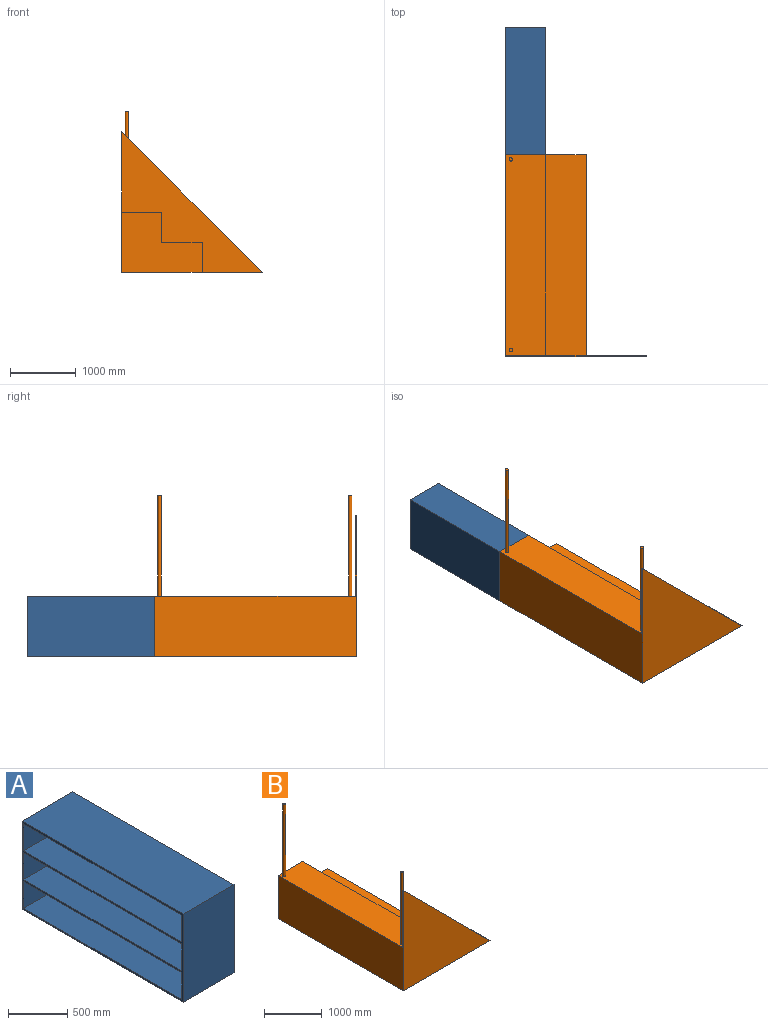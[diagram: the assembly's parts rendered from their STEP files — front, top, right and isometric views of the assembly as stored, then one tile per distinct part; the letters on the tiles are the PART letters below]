
ASSEMBLY  parts=2 mates=1
PART A: 21 faces, bbox 609.6x1930.4x914.4 mm
  f0: plane 1930.4x914.4mm, normal (-1,0,0), area 179031.9mm2, adj f1,f3,f4,f5,f6,f7,f8,f9
  f1: plane 1930.4x609.6mm, normal (0,0,-1), area 1176771.8mm2, adj f0,f2,f4,f5
  f2: plane 1930.4x914.4mm, normal (1,0,0), area 1765157.8mm2, adj f1,f3,f4,f5
  f3: plane 1930.4x609.6mm, normal (0,0,1), area 1176771.8mm2, adj f0,f2,f4,f5
  f4: plane 914.4x609.6mm, normal (0,-1,0), area 557418.2mm2, adj f0,f1,f2,f3
  f5: plane 914.4x609.6mm, normal (0,1,0), area 557418.2mm2, adj f0,f1,f2,f3
  f6: plane 1892.3x590.55mm, normal (0,0,-1), area 1117497.8mm2, adj f0,f7,f9,f10
  f7: plane 590.55x279.4mm, normal (0,-1,0), area 164999.7mm2, adj f0,f6,f8,f10
  f8: plane 1892.3x590.55mm, normal (0,0,1), area 1117497.8mm2, adj f0,f7,f9,f10
  f9: plane 590.55x279.4mm, normal (0,1,0), area 164999.7mm2, adj f0,f6,f8,f10
  f10: plane 1892.3x279.4mm, normal (-1,0,0), area 528708.6mm2, adj f6,f7,f8,f9
  f11: plane 1892.3x590.55mm, normal (0,0,-1), area 1117497.8mm2, adj f0,f12,f14,f15
  f12: plane 590.55x279.4mm, normal (0,-1,0), area 164999.7mm2, adj f0,f11,f13,f15
  f13: plane 1892.3x590.55mm, normal (0,0,1), area 1117497.8mm2, adj f0,f12,f14,f15
  f14: plane 590.55x279.4mm, normal (0,1,0), area 164999.7mm2, adj f0,f11,f13,f15
  f15: plane 1892.3x279.4mm, normal (-1,0,0), area 528708.6mm2, adj f11,f12,f13,f14
  f16: plane 1892.3x590.55mm, normal (0,0,-1), area 1117497.8mm2, adj f0,f17,f19,f20
  f17: plane 590.55x279.4mm, normal (0,-1,0), area 164999.7mm2, adj f0,f16,f18,f20
  f18: plane 1892.3x590.55mm, normal (0,0,1), area 1117497.8mm2, adj f0,f17,f19,f20
  f19: plane 590.55x279.4mm, normal (0,1,0), area 164999.7mm2, adj f0,f16,f18,f20
  f20: plane 1892.3x279.4mm, normal (-1,0,0), area 528708.6mm2, adj f16,f17,f18,f19
PART B: 14 faces, bbox 2133.6x3067.1x2438.4 mm
  f0: plane 3067.05x2133.6mm, normal (-1,0,0), area 2827736.3mm2, adj f1,f5,f6,f11,f12,f13
  f1: plane 3067.05x2133.6mm, normal (0,0,-1), area 3756766.7mm2, adj f0,f2,f6,f11,f12,f13
  f2: plane 3048x457.2mm, normal (1,0,0), area 1393545.6mm2, adj f1,f3,f6,f13
  f3: plane 3048x609.6mm, normal (0,0,1), area 1858060.8mm2, adj f2,f4,f6,f13
  f4: plane 3048x457.2mm, normal (1,0,0), area 1393545.6mm2, adj f3,f5,f6,f13
  f5: plane 3048x609.6mm, normal (0,0,1), area 1854007.1mm2, adj f0,f4,f6,f7,f9,f13
  f6: plane 1219.2x914.4mm, normal (0,1,0), area 836127.4mm2, adj f0,f1,f2,f3,f4,f5
  f7: cylinder r=25.4mm len=1524mm, axis (0,0,-1), area 243219.6mm2, adj f5,f8
  f8: plane 50.8x50.8mm, normal (0,0,1), area 2026.8mm2, adj f7
  f9: cylinder r=25.4mm len=1524mm, axis (0,0,-1), area 243219.6mm2, adj f5,f10
  f10: plane 50.8x50.8mm, normal (0,0,1), area 2026.8mm2, adj f9
  f11: plane 2133.6x2133.6mm, normal (0.71,0,0.71), area 57480.8mm2, adj f0,f1,f12,f13
  f12: plane 2133.6x2133.6mm, normal (0,-1,0), area 2276124.5mm2, adj f0,f1,f11
  f13: plane 2133.6x2133.6mm, normal (0,1,0), area 1439997.1mm2, adj f0,f1,f2,f3,f4,f5,f11
PLACE A rot(axis=(0,0,1),180deg) t=(-2313.57,1105.79,-1285.52)mm
PLACE B rot(axis=(0,0,1),0deg) t=(-1917.86,1105.79,-828.32)mm
MATE fastened B.f6 <-> A.f5  axis (0,1,0) through (-2527.46,1105.79,-1285.52)mm
